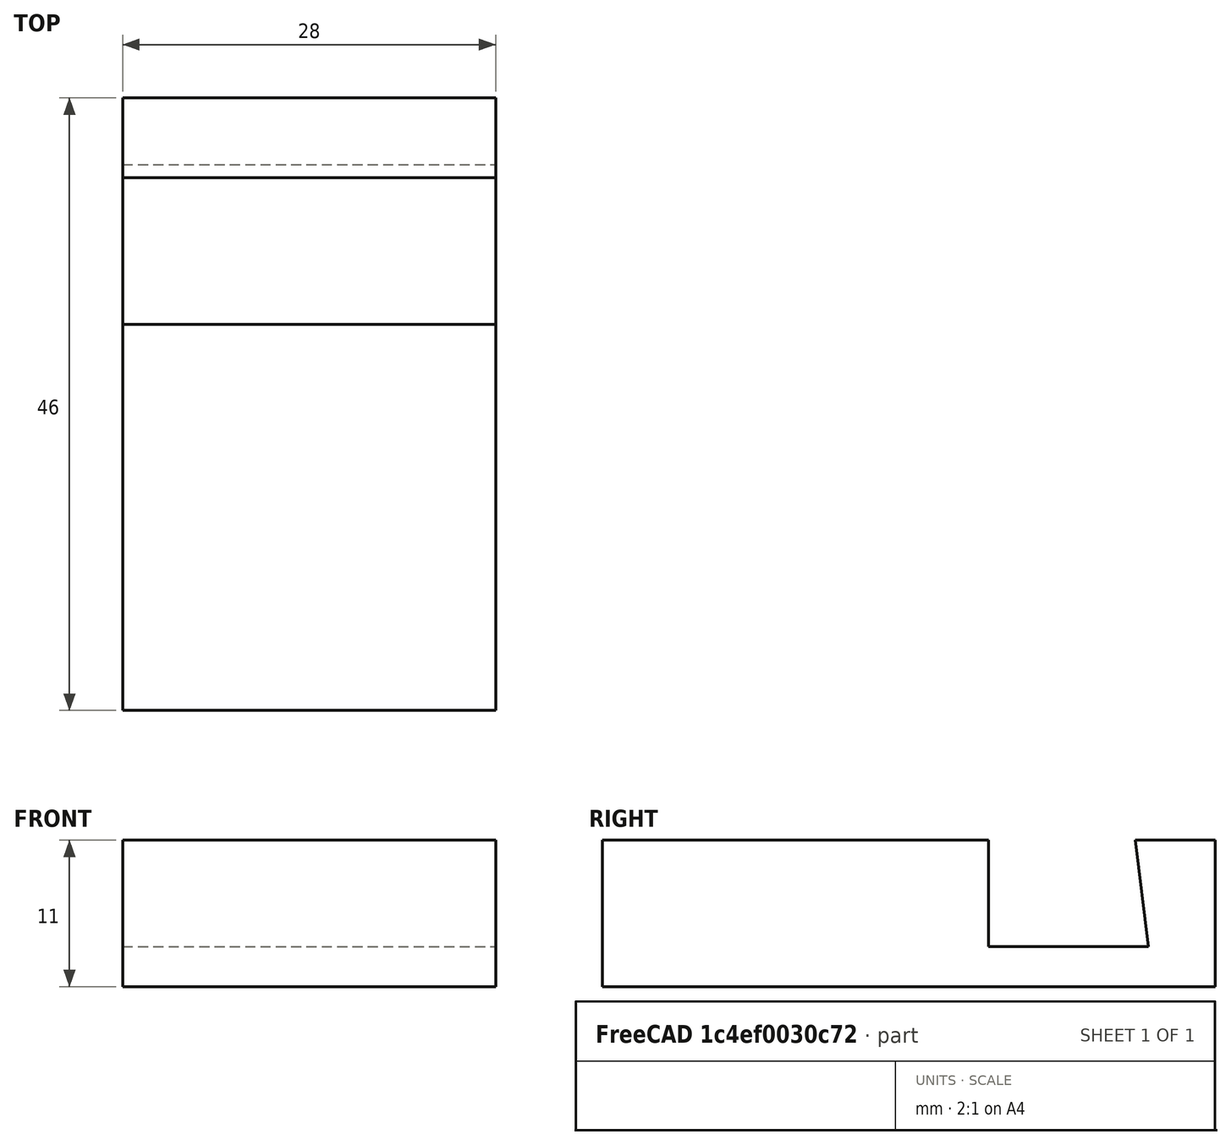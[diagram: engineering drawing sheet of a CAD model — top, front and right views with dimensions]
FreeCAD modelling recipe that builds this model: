
FCSTD DOCUMENT  (FreeCAD 0.16R6707 (Git))
Label: 16-porta-moviles
License: All rights reserved
LicenseURL: http://en.wikipedia.org/wiki/All_rights_reserved
objects: Sketcher::SketchObject×1, PartDesign::Pad×1
note: 3 computed .brp shape members not serialized (recipe doc carries the construction recipe); baked Part::Feature solids carry a one-line shape summary decoded from their .brp

FEATURE [Sketcher::SketchObject] Sketch
  Placement = pos=(0,0,0) rot=(0.57735,0.57735,0.57735;2.0944rad)
  sketch-geometry (8):
    g0: LineSegment StartX=0 StartY=11 StartZ=0 EndX=0 EndY=0 EndZ=0
    g1: LineSegment StartX=0 StartY=0 StartZ=0 EndX=46 EndY=0 EndZ=0
    g2: LineSegment StartX=46 StartY=0 StartZ=0 EndX=46 EndY=11 EndZ=0
    g3: LineSegment StartX=46 StartY=11 StartZ=0 EndX=40 EndY=11 EndZ=0
    g4: LineSegment StartX=40 StartY=11 StartZ=0 EndX=41 EndY=3 EndZ=0
    g5: LineSegment StartX=41 StartY=3 StartZ=0 EndX=29 EndY=3 EndZ=0
    g6: LineSegment StartX=29 StartY=3 StartZ=0 EndX=29 EndY=11 EndZ=0
    g7: LineSegment StartX=29 StartY=11 StartZ=0 EndX=0 EndY=11 EndZ=0
  constraints (23):
    c: Vertical(g0)
    c: Coincident(g0,g1)
    c: Horizontal(g1)
    c: Coincident(g1,g2)
    c: Coincident(g2,g3)
    c: Coincident(g3,g4)
    c: Coincident(g4,g5)
    c: Horizontal(g5)
    c: Coincident(g5,g6)
    c: Vertical(g6)
    c: Coincident(g6,g7)
    c: Coincident(g7,g0)
    c: Horizontal(g7)
    c: DistanceY(g0,g0) = 11
    c: DistanceX(g1,g1) = 46
    c: DistanceX(g7,g7) = 29
    c: DistanceX(g6,g3) = 11
    c: Vertical(g2)
    c: Horizontal(g3)
    c: Equal(g2,g0)
    c: DistanceY(g1,g4) = 3
    c: DistanceX(g5,g5) = 12
    c: Coincident(g0,g-1)
FEATURE [PartDesign::Pad] Pad
  Length = 28
  Length2 = 100
  Midplane = true
  Placement = pos=(0,0,0) rot=(0.57735,0.57735,0.57735;2.0944rad)
  Sketch = -> Sketch
  Type = 0
